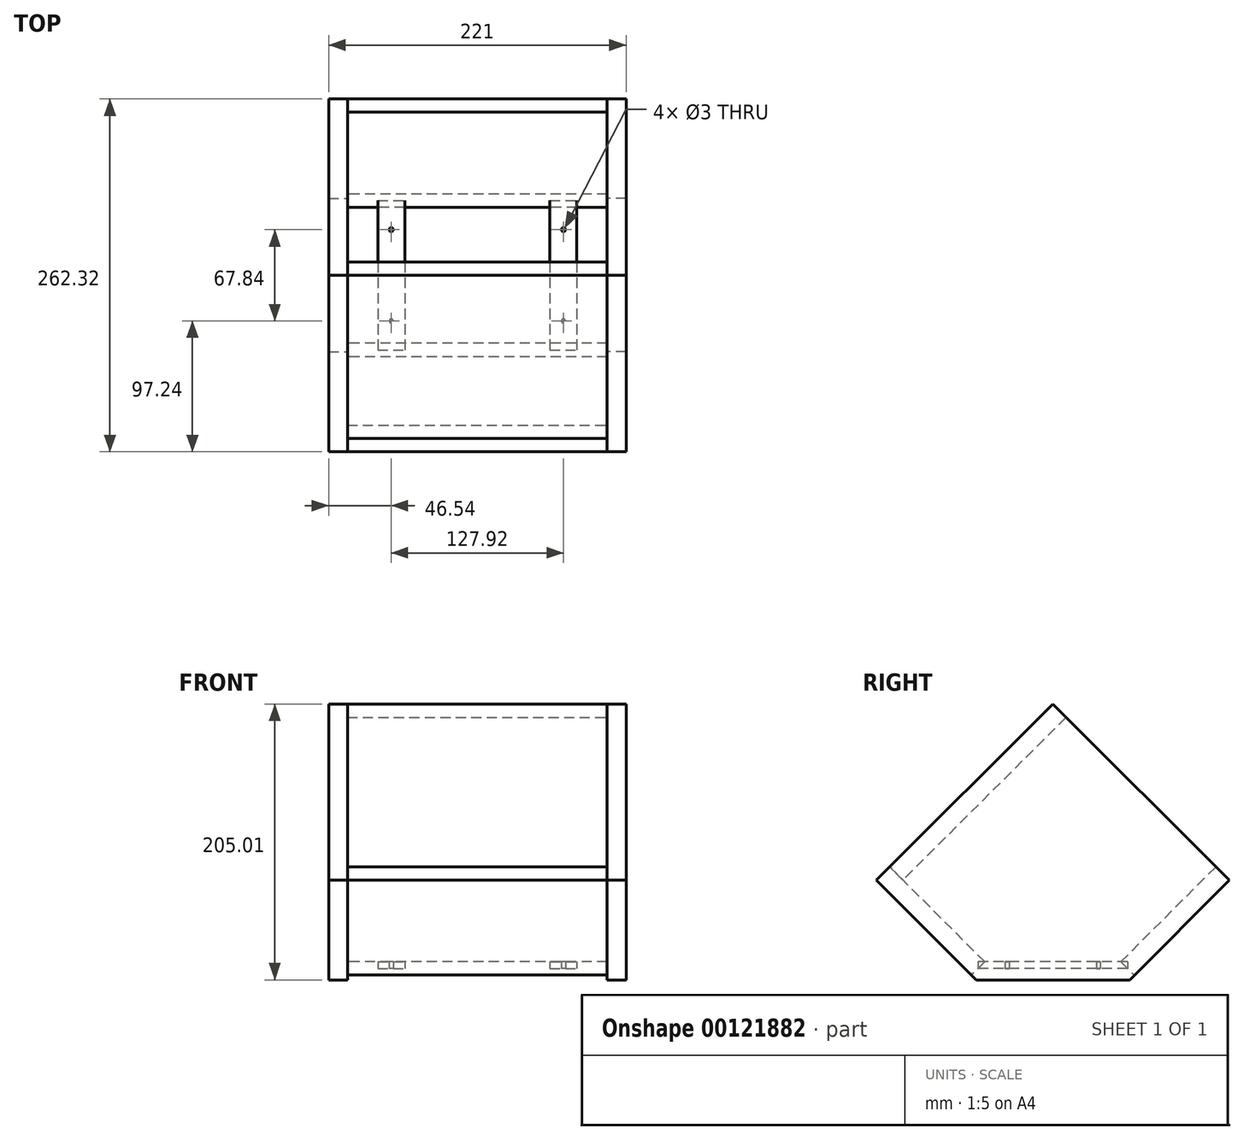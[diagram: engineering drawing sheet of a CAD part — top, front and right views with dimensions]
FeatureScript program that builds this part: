
annotation { "Feature Type Name" : "Feature", "Feature Type Description" : "" }
export const myFeature = defineFeature(function(context is Context, id is Id, definition is map)
    precondition{}
    {
        {
            var Q0;
            Q0=qCreatedBy(makeId("Top.planeOp"),FACE);
            var sketch = newSketch(context, id + "F0", { "sketchPlane" : qUnion([Q0])});
            skLineSegment(sketch, "E0.bottom", {"start": v(-96.5, 55.5) * mm, "end": v(96.5, 55.5) * mm});
            skLineSegment(sketch, "E0.top", {"start": v(-96.5, -55.5) * mm, "end": v(96.5, -55.5) * mm});
            skLineSegment(sketch, "E0.left", {"start": v(-96.5, 55.5) * mm, "end": v(-96.5, -55.5) * mm});
            skLineSegment(sketch, "E0.right", {"start": v(96.5, 55.5) * mm, "end": v(96.5, -55.5) * mm});
            skSolve(sketch);
        }
        {
            var Q0;
            Q0=qSketchRegion(id+"F0",true);
            extrude(context, id + "F1", {"entities" : qUnion([Q0]), "depth" : 8.5 * mm});
        }
        {
            var Q0;
            Q0=makeQuery(id+"F1.opExtrude","CAP_FACE",FACE,{"disambiguationData":[OSD([sQuery(id+"F0.wireOp",EDGE,"E0.bottom"),sQuery(id+"F0.wireOp",EDGE,"E0.top"),sQuery(id+"F0.wireOp",EDGE,"E0.left"),sQuery(id+"F0.wireOp",EDGE,"E0.right")])],"isStart":false});
            var sketch = newSketch(context, id + "F2", { "sketchPlane" : qUnion([Q0])});
            skLineSegment(sketch, "E1.bottom", {"start": v(-73.96, 55.5) * mm, "end": v(-53.96, 55.5) * mm});
            skLineSegment(sketch, "E1.top", {"start": v(-73.96, -55.5) * mm, "end": v(-53.96, -55.5) * mm});
            skLineSegment(sketch, "E1.left", {"start": v(-73.96, 55.5) * mm, "end": v(-73.96, -55.5) * mm});
            skLineSegment(sketch, "E1.right", {"start": v(-53.96, 55.5) * mm, "end": v(-53.96, -55.5) * mm});
            skLineSegment(sketch, "E2.bottom", {"start": v(53.96, 55.5) * mm, "end": v(73.96, 55.5) * mm});
            skLineSegment(sketch, "E2.top", {"start": v(53.96, -55.5) * mm, "end": v(73.96, -55.5) * mm});
            skLineSegment(sketch, "E2.left", {"start": v(53.96, 55.5) * mm, "end": v(53.96, -55.5) * mm});
            skLineSegment(sketch, "E2.right", {"start": v(73.96, 55.5) * mm, "end": v(73.96, -55.5) * mm});
            skSolve(sketch);
        }
        {
            var Q0;
            Q0=qSketchRegion(id+"F2",true);
            extrude(context, id + "F3", {"entities" : qUnion([Q0]), "depth" : 5 * mm});
        }
        {
            var Q0;
            Q0=makeQuery(id+"F1.opExtrude","CAP_FACE",FACE,{"disambiguationData":[OSD([sQuery(id+"F0.wireOp",EDGE,"E0.bottom"),sQuery(id+"F0.wireOp",EDGE,"E0.top"),sQuery(id+"F0.wireOp",EDGE,"E0.left"),sQuery(id+"F0.wireOp",EDGE,"E0.right")])],"isStart":false});
            var sketch = newSketch(context, id + "F4", { "sketchPlane" : qUnion([Q0])});
            skCircle(sketch, "E3", {"center": v(-63.96, 33.92) * mm, "radius": 1.5 * mm});
            skCircle(sketch, "E4", {"center": v(63.96, 33.92) * mm, "radius": 1.5 * mm});
            skCircle(sketch, "E5", {"center": v(-63.96, -33.92) * mm, "radius": 1.5 * mm});
            skCircle(sketch, "E6", {"center": v(63.96, -33.92) * mm, "radius": 1.5 * mm});
            skSolve(sketch);
        }
        {
            var Q0;
            Q0=qSketchRegion(id+"F4",true);
            extrude(context, id + "F5", {"entities" : qUnion([Q0]), "operationType" : NewBodyOperationType.REMOVE, "endBound" : BoundingType.THROUGH_ALL, "depth" : 2.5 * mm, "hasSecondDirection" : true, "secondDirectionOppositeDirection" : true, "secondDirectionDepth" : 2.5 * mm});
        }
        {
            var Q0;
            {var subQ0=sQuery(id+"F0.wireOp",EDGE,"E0.top");Q0=makeQuery(id+"F3.boolean.opBoolean","SPLIT",EDGE,{"disambiguationData":[TD([makeQuery(id+"F3.opExtrude","SWEPT_FACE",FACE,{"disambiguationData":[OSD([sQuery(id+"F2.wireOp",EDGE,"E1.right")])]})])],"derivedFrom":makeQuery(id+"F1.opExtrude","CAP_EDGE",EDGE,{"disambiguationData":[OSD([subQ0])],"isStart":false})});}
            cPlane(context, id + "F6", {"entities" : qUnion([Q0]), "cplaneType" : CPlaneType.LINE_ANGLE, "offset" : 25 * mm, "angle" : 45 * degree, "width" : 150 * mm, "height" : 150 * mm});
        }
        {
            var Q0;
            Q0=qCreatedBy(id+"F6.planeOp",FACE);
            var sketch = newSketch(context, id + "F7", { "sketchPlane" : qUnion([Q0])});
            skLineSegment(sketch, "E7.bottom", {"start": v(-96.5, 45.25) * mm, "end": v(96.5, 45.25) * mm});
            skLineSegment(sketch, "E7.top", {"start": v(-96.5, 145.25) * mm, "end": v(96.5, 145.25) * mm});
            skLineSegment(sketch, "E7.left", {"start": v(-96.5, 45.25) * mm, "end": v(-96.5, 145.25) * mm});
            skLineSegment(sketch, "E7.right", {"start": v(96.5, 45.25) * mm, "end": v(96.5, 145.25) * mm});
            skSolve(sketch);
        }
        {
            var Q0;
            Q0=qSketchRegion(id+"F7",true);
            extrude(context, id + "F8", {"entities" : qUnion([Q0]), "endBound" : BoundingType.SYMMETRIC, "depth" : 14 * mm});
        }
        {
            var Q0;
            Q0=makeQuery(id+"F8.opExtrude","SWEPT_BODY",BODY,{"disambiguationData":[OSD([sQuery(id+"F7.wireOp",EDGE,"E7.bottom"),sQuery(id+"F7.wireOp",EDGE,"E7.top"),sQuery(id+"F7.wireOp",EDGE,"E7.left"),sQuery(id+"F7.wireOp",EDGE,"E7.right")])]});
            var Q1;
            Q1=qCreatedBy(makeId("Front.planeOp"),FACE);
            mirror(context, id + "F9", {"entities" : qUnion([Q0]), "mirrorPlane" : qUnion([Q1])});
        }
        {
            var Q0;
            Q0=makeQuery(id+"F8.opExtrude","SWEPT_FACE",FACE,{"disambiguationData":[OSD([sQuery(id+"F7.wireOp",EDGE,"E7.right")])]});
            var sketch = newSketch(context, id + "F10", { "sketchPlane" : qUnion([Q0])});
            skLineSegment(sketch, "E8", {"start": v(131.16, 74.26) * mm, "end": v(56.9, 0) * mm});
            skLineSegment(sketch, "E9", {"start": v(-131.16, 74.26) * mm, "end": v(-57.13, 0) * mm});
            skLineSegment(sketch, "E10", {"start": v(-57.13, 0) * mm, "end": v(56.9, 0) * mm});
            skLineSegment(sketch, "E11", {"start": v(-131.16, 74.26) * mm, "end": v(0, 205) * mm});
            skLineSegment(sketch, "E12", {"start": v(0, 205) * mm, "end": v(131.16, 74.26) * mm});
            skSolve(sketch);
        }
        {
            var Q0;
            Q0=qSketchRegion(id+"F10",true);
            extrude(context, id + "F11", {"entities" : qUnion([Q0]), "depth" : 14 * mm});
        }
        {
            var Q0;
            Q0=makeQuery(id+"F11.opExtrude","SWEPT_BODY",BODY,{"disambiguationData":[OSD([sQuery(id+"F10.wireOp",EDGE,"E8"),sQuery(id+"F10.wireOp",EDGE,"E9"),sQuery(id+"F10.wireOp",EDGE,"E10"),sQuery(id+"F10.wireOp",EDGE,"E11"),sQuery(id+"F10.wireOp",EDGE,"E12")])]});
            var Q1;
            Q1=qCreatedBy(makeId("Right.planeOp"),FACE);
            mirror(context, id + "F12", {"entities" : qUnion([Q0]), "mirrorPlane" : qUnion([Q1])});
        }
        {
            var Q0;
            Q0=makeQuery(id+"F11.opExtrude","SWEPT_FACE",FACE,{"disambiguationData":[OSD([sQuery(id+"F10.wireOp",EDGE,"E12")])]});
            var sketch = newSketch(context, id + "F13", { "sketchPlane" : qUnion([Q0])});
            skLineSegment(sketch, "E13.bottom", {"start": v(-96.5, 144.74) * mm, "end": v(96.5, 144.74) * mm});
            skLineSegment(sketch, "E13.top", {"start": v(-96.5, -26.46) * mm, "end": v(96.5, -26.46) * mm});
            skLineSegment(sketch, "E13.left", {"start": v(-96.5, 144.74) * mm, "end": v(-96.5, -26.46) * mm});
            skLineSegment(sketch, "E13.right", {"start": v(96.5, 144.74) * mm, "end": v(96.5, -26.46) * mm});
            skSolve(sketch);
        }
        {
            var Q0;
            Q0=qSketchRegion(id+"F13",true);
            extrude(context, id + "F14", {"entities" : qUnion([Q0]), "oppositeDirection" : true, "depth" : 14 * mm});
        }
        {
            var Q0;
            Q0=makeQuery(id+"F1.opExtrude","SWEPT_BODY",BODY,{"disambiguationData":[OSD([sQuery(id+"F0.wireOp",EDGE,"E0.bottom"),sQuery(id+"F0.wireOp",EDGE,"E0.top"),sQuery(id+"F0.wireOp",EDGE,"E0.left"),sQuery(id+"F0.wireOp",EDGE,"E0.right")])]});
            deleteBodies(context, id + "F15", {"entities" : qUnion([Q0])});
        }
    });
